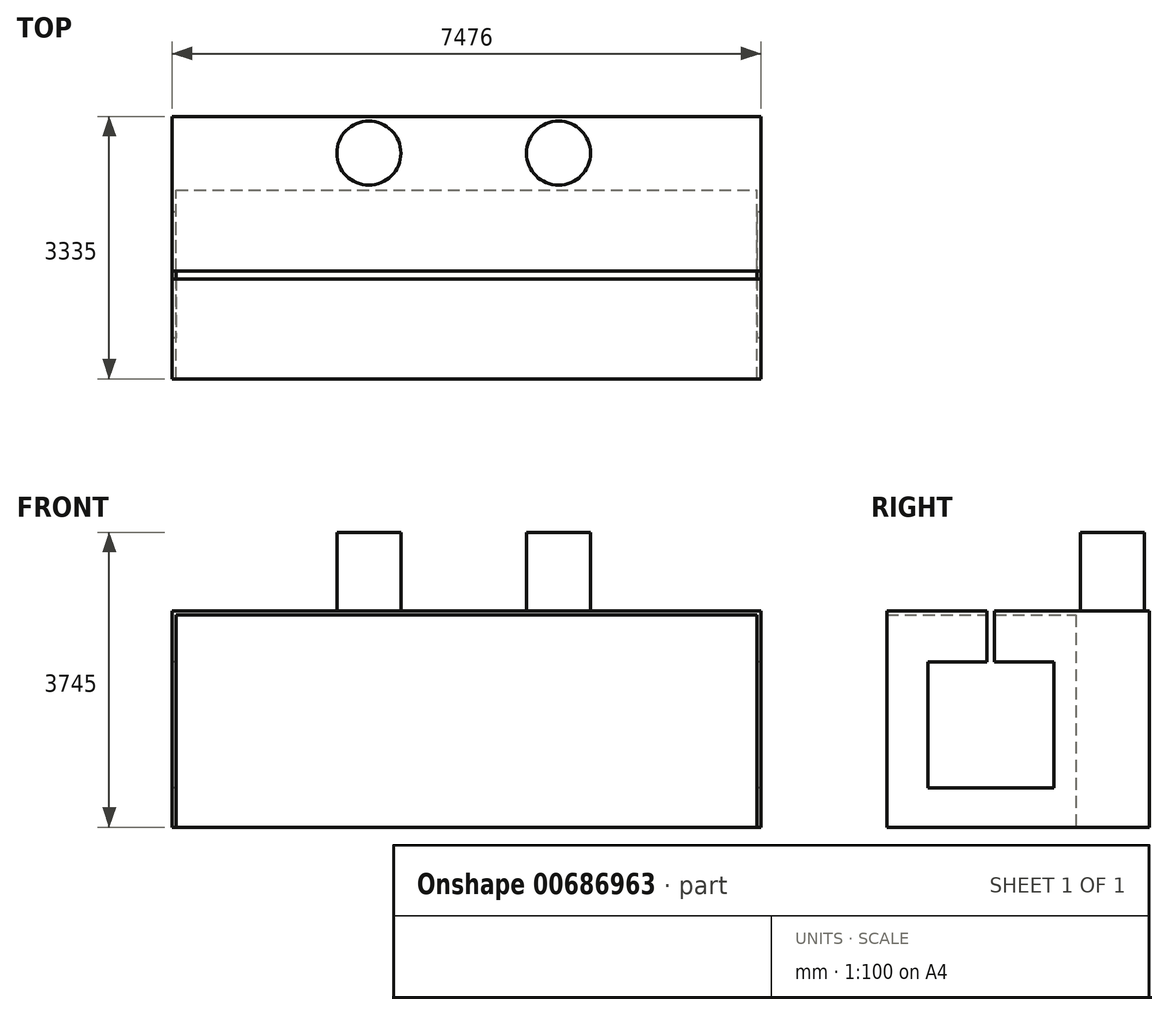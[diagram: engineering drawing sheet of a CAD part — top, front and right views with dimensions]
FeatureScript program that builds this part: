
annotation { "Feature Type Name" : "Feature", "Feature Type Description" : "" }
export const myFeature = defineFeature(function(context is Context, id is Id, definition is map)
    precondition{}
    {
        {
            var Q0;
            Q0=qCreatedBy(makeId("Front.planeOp"),FACE);
            var sketch = newSketch(context, id + "F0", { "sketchPlane" : qUnion([Q0])});
            skLineSegment(sketch, "E0.bottom", {"start": v(0, 0) * mm, "end": v(7476, 0) * mm});
            skLineSegment(sketch, "E0.top", {"start": v(0, 2745) * mm, "end": v(7476, 2745) * mm});
            skLineSegment(sketch, "E0.left", {"start": v(0, 0) * mm, "end": v(0, 2745) * mm});
            skLineSegment(sketch, "E0.right", {"start": v(7476, 0) * mm, "end": v(7476, 2745) * mm});
            skSolve(sketch);
        }
        {
            var Q0;
            Q0=makeQuery(id+"F0.imprint","IMPRINT",FACE,{"disambiguationData":[TD([[makeQuery(id+"F0.imprint","IMPRINT",EDGE,{"derivedFrom":sQuery(id+"F0.wireOp",EDGE,"E0.bottom")}),1.0]])]});
            extrude(context, id + "F1", {"entities" : qUnion([Q0]), "depth" : 935 * mm, "offsetDistance" : 25 * mm});
        }
        {
            var Q0;
            Q0=makeQuery(id+"F1.opExtrude","CAP_FACE",FACE,{"disambiguationData":[OSD([sQuery(id+"F0.wireOp",EDGE,"E0.bottom"),sQuery(id+"F0.wireOp",EDGE,"E0.top"),sQuery(id+"F0.wireOp",EDGE,"E0.left"),sQuery(id+"F0.wireOp",EDGE,"E0.right")])],"isStart":false});
            var sketch = newSketch(context, id + "F2", { "sketchPlane" : qUnion([Q0])});
            skLineSegment(sketch, "E1.bottom", {"start": v(38, 2050) * mm, "end": v(2438, 2050) * mm});
            skLineSegment(sketch, "E1.top", {"start": v(38, 250) * mm, "end": v(2438, 250) * mm});
            skLineSegment(sketch, "E1.left", {"start": v(38, 2050) * mm, "end": v(38, 250) * mm});
            skLineSegment(sketch, "E1.right", {"start": v(2438, 2050) * mm, "end": v(2438, 250) * mm});
            skLineSegment(sketch, "E2.1.0.0", {"start": v(2538, 250) * mm, "end": v(4938, 250) * mm});
            skLineSegment(sketch, "E2.1.0.1", {"start": v(2538, 2050) * mm, "end": v(4938, 2050) * mm});
            skLineSegment(sketch, "E2.1.0.2", {"start": v(4938, 2050) * mm, "end": v(4938, 250) * mm});
            skLineSegment(sketch, "E2.1.0.3", {"start": v(2538, 2050) * mm, "end": v(2538, 250) * mm});
            skLineSegment(sketch, "E2.2.0.0", {"start": v(5038, 250) * mm, "end": v(7438, 250) * mm});
            skLineSegment(sketch, "E2.2.0.1", {"start": v(5038, 2050) * mm, "end": v(7438, 2050) * mm});
            skLineSegment(sketch, "E2.2.0.2", {"start": v(7438, 2050) * mm, "end": v(7438, 250) * mm});
            skLineSegment(sketch, "E2.2.0.3", {"start": v(5038, 2050) * mm, "end": v(5038, 250) * mm});
            skLineSegment(sketch, "E2.direction1", {"start": v(38, 2050) * mm, "end": v(2538, 2050) * mm, "construction": true});
            skLineSegment(sketch, "E3.1.0.0", {"start": v(63, 2050) * mm, "end": v(63, 250) * mm});
            skLineSegment(sketch, "E3.2.0.0", {"start": v(88, 2050) * mm, "end": v(88, 250) * mm});
            skLineSegment(sketch, "E3.3.0.0", {"start": v(113, 2050) * mm, "end": v(113, 250) * mm});
            skLineSegment(sketch, "E3.4.0.0", {"start": v(138, 2050) * mm, "end": v(138, 250) * mm});
            skLineSegment(sketch, "E3.5.0.0", {"start": v(163, 2050) * mm, "end": v(163, 250) * mm});
            skLineSegment(sketch, "E3.6.0.0", {"start": v(188, 2050) * mm, "end": v(188, 250) * mm});
            skLineSegment(sketch, "E3.7.0.0", {"start": v(213, 2050) * mm, "end": v(213, 250) * mm});
            skLineSegment(sketch, "E3.8.0.0", {"start": v(238, 2050) * mm, "end": v(238, 250) * mm});
            skLineSegment(sketch, "E3.9.0.0", {"start": v(263, 2050) * mm, "end": v(263, 250) * mm});
            skLineSegment(sketch, "E3.10.0.0", {"start": v(288, 2050) * mm, "end": v(288, 250) * mm});
            skLineSegment(sketch, "E3.11.0.0", {"start": v(313, 2050) * mm, "end": v(313, 250) * mm});
            skLineSegment(sketch, "E3.12.0.0", {"start": v(338, 2050) * mm, "end": v(338, 250) * mm});
            skLineSegment(sketch, "E3.13.0.0", {"start": v(363, 2050) * mm, "end": v(363, 250) * mm});
            skLineSegment(sketch, "E3.14.0.0", {"start": v(388, 2050) * mm, "end": v(388, 250) * mm});
            skLineSegment(sketch, "E3.15.0.0", {"start": v(413, 2050) * mm, "end": v(413, 250) * mm});
            skLineSegment(sketch, "E3.16.0.0", {"start": v(438, 2050) * mm, "end": v(438, 250) * mm});
            skLineSegment(sketch, "E3.17.0.0", {"start": v(463, 2050) * mm, "end": v(463, 250) * mm});
            skLineSegment(sketch, "E3.18.0.0", {"start": v(488, 2050) * mm, "end": v(488, 250) * mm});
            skLineSegment(sketch, "E3.19.0.0", {"start": v(513, 2050) * mm, "end": v(513, 250) * mm});
            skLineSegment(sketch, "E3.20.0.0", {"start": v(538, 2050) * mm, "end": v(538, 250) * mm});
            skLineSegment(sketch, "E3.21.0.0", {"start": v(563, 2050) * mm, "end": v(563, 250) * mm});
            skLineSegment(sketch, "E3.22.0.0", {"start": v(588, 2050) * mm, "end": v(588, 250) * mm});
            skLineSegment(sketch, "E3.23.0.0", {"start": v(613, 2050) * mm, "end": v(613, 250) * mm});
            skLineSegment(sketch, "E3.24.0.0", {"start": v(638, 2050) * mm, "end": v(638, 250) * mm});
            skLineSegment(sketch, "E3.25.0.0", {"start": v(663, 2050) * mm, "end": v(663, 250) * mm});
            skLineSegment(sketch, "E3.26.0.0", {"start": v(688, 2050) * mm, "end": v(688, 250) * mm});
            skLineSegment(sketch, "E3.27.0.0", {"start": v(713, 2050) * mm, "end": v(713, 250) * mm});
            skLineSegment(sketch, "E3.28.0.0", {"start": v(738, 2050) * mm, "end": v(738, 250) * mm});
            skLineSegment(sketch, "E3.29.0.0", {"start": v(763, 2050) * mm, "end": v(763, 250) * mm});
            skLineSegment(sketch, "E3.30.0.0", {"start": v(788, 2050) * mm, "end": v(788, 250) * mm});
            skLineSegment(sketch, "E3.31.0.0", {"start": v(813, 2050) * mm, "end": v(813, 250) * mm});
            skLineSegment(sketch, "E3.32.0.0", {"start": v(838, 2050) * mm, "end": v(838, 250) * mm});
            skLineSegment(sketch, "E3.33.0.0", {"start": v(863, 2050) * mm, "end": v(863, 250) * mm});
            skLineSegment(sketch, "E3.34.0.0", {"start": v(888, 2050) * mm, "end": v(888, 250) * mm});
            skLineSegment(sketch, "E3.35.0.0", {"start": v(913, 2050) * mm, "end": v(913, 250) * mm});
            skLineSegment(sketch, "E3.36.0.0", {"start": v(938, 2050) * mm, "end": v(938, 250) * mm});
            skLineSegment(sketch, "E3.37.0.0", {"start": v(963, 2050) * mm, "end": v(963, 250) * mm});
            skLineSegment(sketch, "E3.38.0.0", {"start": v(988, 2050) * mm, "end": v(988, 250) * mm});
            skLineSegment(sketch, "E3.39.0.0", {"start": v(1013, 2050) * mm, "end": v(1013, 250) * mm});
            skLineSegment(sketch, "E3.40.0.0", {"start": v(1038, 2050) * mm, "end": v(1038, 250) * mm});
            skLineSegment(sketch, "E3.41.0.0", {"start": v(1063, 2050) * mm, "end": v(1063, 250) * mm});
            skLineSegment(sketch, "E3.42.0.0", {"start": v(1088, 2050) * mm, "end": v(1088, 250) * mm});
            skLineSegment(sketch, "E3.43.0.0", {"start": v(1113, 2050) * mm, "end": v(1113, 250) * mm});
            skLineSegment(sketch, "E3.44.0.0", {"start": v(1138, 2050) * mm, "end": v(1138, 250) * mm});
            skLineSegment(sketch, "E3.45.0.0", {"start": v(1163, 2050) * mm, "end": v(1163, 250) * mm});
            skLineSegment(sketch, "E3.46.0.0", {"start": v(1188, 2050) * mm, "end": v(1188, 250) * mm});
            skLineSegment(sketch, "E3.47.0.0", {"start": v(1213, 2050) * mm, "end": v(1213, 250) * mm});
            skLineSegment(sketch, "E3.48.0.0", {"start": v(1238, 2050) * mm, "end": v(1238, 250) * mm});
            skLineSegment(sketch, "E3.49.0.0", {"start": v(1263, 2050) * mm, "end": v(1263, 250) * mm});
            skLineSegment(sketch, "E3.50.0.0", {"start": v(1288, 2050) * mm, "end": v(1288, 250) * mm});
            skLineSegment(sketch, "E3.51.0.0", {"start": v(1313, 2050) * mm, "end": v(1313, 250) * mm});
            skLineSegment(sketch, "E3.52.0.0", {"start": v(1338, 2050) * mm, "end": v(1338, 250) * mm});
            skLineSegment(sketch, "E3.53.0.0", {"start": v(1363, 2050) * mm, "end": v(1363, 250) * mm});
            skLineSegment(sketch, "E3.54.0.0", {"start": v(1388, 2050) * mm, "end": v(1388, 250) * mm});
            skLineSegment(sketch, "E3.55.0.0", {"start": v(1413, 2050) * mm, "end": v(1413, 250) * mm});
            skLineSegment(sketch, "E3.56.0.0", {"start": v(1438, 2050) * mm, "end": v(1438, 250) * mm});
            skLineSegment(sketch, "E3.57.0.0", {"start": v(1463, 2050) * mm, "end": v(1463, 250) * mm});
            skLineSegment(sketch, "E3.58.0.0", {"start": v(1488, 2050) * mm, "end": v(1488, 250) * mm});
            skLineSegment(sketch, "E3.59.0.0", {"start": v(1513, 2050) * mm, "end": v(1513, 250) * mm});
            skLineSegment(sketch, "E3.60.0.0", {"start": v(1538, 2050) * mm, "end": v(1538, 250) * mm});
            skLineSegment(sketch, "E3.61.0.0", {"start": v(1563, 2050) * mm, "end": v(1563, 250) * mm});
            skLineSegment(sketch, "E3.62.0.0", {"start": v(1588, 2050) * mm, "end": v(1588, 250) * mm});
            skLineSegment(sketch, "E3.63.0.0", {"start": v(1613, 2050) * mm, "end": v(1613, 250) * mm});
            skLineSegment(sketch, "E3.64.0.0", {"start": v(1638, 2050) * mm, "end": v(1638, 250) * mm});
            skLineSegment(sketch, "E3.65.0.0", {"start": v(1663, 2050) * mm, "end": v(1663, 250) * mm});
            skLineSegment(sketch, "E3.66.0.0", {"start": v(1688, 2050) * mm, "end": v(1688, 250) * mm});
            skLineSegment(sketch, "E3.67.0.0", {"start": v(1713, 2050) * mm, "end": v(1713, 250) * mm});
            skLineSegment(sketch, "E3.68.0.0", {"start": v(1738, 2050) * mm, "end": v(1738, 250) * mm});
            skLineSegment(sketch, "E3.69.0.0", {"start": v(1763, 2050) * mm, "end": v(1763, 250) * mm});
            skLineSegment(sketch, "E3.70.0.0", {"start": v(1788, 2050) * mm, "end": v(1788, 250) * mm});
            skLineSegment(sketch, "E3.71.0.0", {"start": v(1813, 2050) * mm, "end": v(1813, 250) * mm});
            skLineSegment(sketch, "E3.72.0.0", {"start": v(1838, 2050) * mm, "end": v(1838, 250) * mm});
            skLineSegment(sketch, "E3.73.0.0", {"start": v(1863, 2050) * mm, "end": v(1863, 250) * mm});
            skLineSegment(sketch, "E3.74.0.0", {"start": v(1888, 2050) * mm, "end": v(1888, 250) * mm});
            skLineSegment(sketch, "E3.75.0.0", {"start": v(1913, 2050) * mm, "end": v(1913, 250) * mm});
            skLineSegment(sketch, "E3.76.0.0", {"start": v(1938, 2050) * mm, "end": v(1938, 250) * mm});
            skLineSegment(sketch, "E3.77.0.0", {"start": v(1963, 2050) * mm, "end": v(1963, 250) * mm});
            skLineSegment(sketch, "E3.78.0.0", {"start": v(1988, 2050) * mm, "end": v(1988, 250) * mm});
            skLineSegment(sketch, "E3.79.0.0", {"start": v(2013, 2050) * mm, "end": v(2013, 250) * mm});
            skLineSegment(sketch, "E3.80.0.0", {"start": v(2038, 2050) * mm, "end": v(2038, 250) * mm});
            skLineSegment(sketch, "E3.81.0.0", {"start": v(2063, 2050) * mm, "end": v(2063, 250) * mm});
            skLineSegment(sketch, "E3.82.0.0", {"start": v(2088, 2050) * mm, "end": v(2088, 250) * mm});
            skLineSegment(sketch, "E3.83.0.0", {"start": v(2113, 2050) * mm, "end": v(2113, 250) * mm});
            skLineSegment(sketch, "E3.84.0.0", {"start": v(2138, 2050) * mm, "end": v(2138, 250) * mm});
            skLineSegment(sketch, "E3.85.0.0", {"start": v(2163, 2050) * mm, "end": v(2163, 250) * mm});
            skLineSegment(sketch, "E3.86.0.0", {"start": v(2188, 2050) * mm, "end": v(2188, 250) * mm});
            skLineSegment(sketch, "E3.87.0.0", {"start": v(2213, 2050) * mm, "end": v(2213, 250) * mm});
            skLineSegment(sketch, "E3.88.0.0", {"start": v(2238, 2050) * mm, "end": v(2238, 250) * mm});
            skLineSegment(sketch, "E3.89.0.0", {"start": v(2263, 2050) * mm, "end": v(2263, 250) * mm});
            skLineSegment(sketch, "E3.90.0.0", {"start": v(2288, 2050) * mm, "end": v(2288, 250) * mm});
            skLineSegment(sketch, "E3.91.0.0", {"start": v(2313, 2050) * mm, "end": v(2313, 250) * mm});
            skLineSegment(sketch, "E3.92.0.0", {"start": v(2338, 2050) * mm, "end": v(2338, 250) * mm});
            skLineSegment(sketch, "E3.93.0.0", {"start": v(2363, 2050) * mm, "end": v(2363, 250) * mm});
            skLineSegment(sketch, "E3.94.0.0", {"start": v(2388, 2050) * mm, "end": v(2388, 250) * mm});
            skLineSegment(sketch, "E3.direction1", {"start": v(38, 250) * mm, "end": v(63, 250) * mm, "construction": true});
            skLineSegment(sketch, "E4.0.95.0", {"start": v(2413, 2050) * mm, "end": v(2413, 250) * mm});
            skLineSegment(sketch, "E5.1.0.0", {"start": v(5063, 2050) * mm, "end": v(5063, 250) * mm});
            skLineSegment(sketch, "E5.2.0.0", {"start": v(5088, 2050) * mm, "end": v(5088, 250) * mm});
            skLineSegment(sketch, "E5.3.0.0", {"start": v(5113, 2050) * mm, "end": v(5113, 250) * mm});
            skLineSegment(sketch, "E5.4.0.0", {"start": v(5138, 2050) * mm, "end": v(5138, 250) * mm});
            skLineSegment(sketch, "E5.5.0.0", {"start": v(5163, 2050) * mm, "end": v(5163, 250) * mm});
            skLineSegment(sketch, "E5.6.0.0", {"start": v(5188, 2050) * mm, "end": v(5188, 250) * mm});
            skLineSegment(sketch, "E5.7.0.0", {"start": v(5213, 2050) * mm, "end": v(5213, 250) * mm});
            skLineSegment(sketch, "E5.8.0.0", {"start": v(5238, 2050) * mm, "end": v(5238, 250) * mm});
            skLineSegment(sketch, "E5.9.0.0", {"start": v(5263, 2050) * mm, "end": v(5263, 250) * mm});
            skLineSegment(sketch, "E5.10.0.0", {"start": v(5288, 2050) * mm, "end": v(5288, 250) * mm});
            skLineSegment(sketch, "E5.11.0.0", {"start": v(5313, 2050) * mm, "end": v(5313, 250) * mm});
            skLineSegment(sketch, "E5.12.0.0", {"start": v(5338, 2050) * mm, "end": v(5338, 250) * mm});
            skLineSegment(sketch, "E5.13.0.0", {"start": v(5363, 2050) * mm, "end": v(5363, 250) * mm});
            skLineSegment(sketch, "E5.14.0.0", {"start": v(5388, 2050) * mm, "end": v(5388, 250) * mm});
            skLineSegment(sketch, "E5.15.0.0", {"start": v(5413, 2050) * mm, "end": v(5413, 250) * mm});
            skLineSegment(sketch, "E5.16.0.0", {"start": v(5438, 2050) * mm, "end": v(5438, 250) * mm});
            skLineSegment(sketch, "E5.17.0.0", {"start": v(5463, 2050) * mm, "end": v(5463, 250) * mm});
            skLineSegment(sketch, "E5.18.0.0", {"start": v(5488, 2050) * mm, "end": v(5488, 250) * mm});
            skLineSegment(sketch, "E5.19.0.0", {"start": v(5513, 2050) * mm, "end": v(5513, 250) * mm});
            skLineSegment(sketch, "E5.20.0.0", {"start": v(5538, 2050) * mm, "end": v(5538, 250) * mm});
            skLineSegment(sketch, "E5.21.0.0", {"start": v(5563, 2050) * mm, "end": v(5563, 250) * mm});
            skLineSegment(sketch, "E5.22.0.0", {"start": v(5588, 2050) * mm, "end": v(5588, 250) * mm});
            skLineSegment(sketch, "E5.23.0.0", {"start": v(5613, 2050) * mm, "end": v(5613, 250) * mm});
            skLineSegment(sketch, "E5.24.0.0", {"start": v(5638, 2050) * mm, "end": v(5638, 250) * mm});
            skLineSegment(sketch, "E5.25.0.0", {"start": v(5663, 2050) * mm, "end": v(5663, 250) * mm});
            skLineSegment(sketch, "E5.26.0.0", {"start": v(5688, 2050) * mm, "end": v(5688, 250) * mm});
            skLineSegment(sketch, "E5.27.0.0", {"start": v(5713, 2050) * mm, "end": v(5713, 250) * mm});
            skLineSegment(sketch, "E5.28.0.0", {"start": v(5738, 2050) * mm, "end": v(5738, 250) * mm});
            skLineSegment(sketch, "E5.29.0.0", {"start": v(5763, 2050) * mm, "end": v(5763, 250) * mm});
            skLineSegment(sketch, "E5.30.0.0", {"start": v(5788, 2050) * mm, "end": v(5788, 250) * mm});
            skLineSegment(sketch, "E5.31.0.0", {"start": v(5813, 2050) * mm, "end": v(5813, 250) * mm});
            skLineSegment(sketch, "E5.32.0.0", {"start": v(5838, 2050) * mm, "end": v(5838, 250) * mm});
            skLineSegment(sketch, "E5.33.0.0", {"start": v(5863, 2050) * mm, "end": v(5863, 250) * mm});
            skLineSegment(sketch, "E5.34.0.0", {"start": v(5888, 2050) * mm, "end": v(5888, 250) * mm});
            skLineSegment(sketch, "E5.35.0.0", {"start": v(5913, 2050) * mm, "end": v(5913, 250) * mm});
            skLineSegment(sketch, "E5.36.0.0", {"start": v(5938, 2050) * mm, "end": v(5938, 250) * mm});
            skLineSegment(sketch, "E5.37.0.0", {"start": v(5963, 2050) * mm, "end": v(5963, 250) * mm});
            skLineSegment(sketch, "E5.38.0.0", {"start": v(5988, 2050) * mm, "end": v(5988, 250) * mm});
            skLineSegment(sketch, "E5.39.0.0", {"start": v(6013, 2050) * mm, "end": v(6013, 250) * mm});
            skLineSegment(sketch, "E5.40.0.0", {"start": v(6038, 2050) * mm, "end": v(6038, 250) * mm});
            skLineSegment(sketch, "E5.41.0.0", {"start": v(6063, 2050) * mm, "end": v(6063, 250) * mm});
            skLineSegment(sketch, "E5.42.0.0", {"start": v(6088, 2050) * mm, "end": v(6088, 250) * mm});
            skLineSegment(sketch, "E5.43.0.0", {"start": v(6113, 2050) * mm, "end": v(6113, 250) * mm});
            skLineSegment(sketch, "E5.44.0.0", {"start": v(6138, 2050) * mm, "end": v(6138, 250) * mm});
            skLineSegment(sketch, "E5.45.0.0", {"start": v(6163, 2050) * mm, "end": v(6163, 250) * mm});
            skLineSegment(sketch, "E5.46.0.0", {"start": v(6188, 2050) * mm, "end": v(6188, 250) * mm});
            skLineSegment(sketch, "E5.47.0.0", {"start": v(6213, 2050) * mm, "end": v(6213, 250) * mm});
            skLineSegment(sketch, "E5.48.0.0", {"start": v(6238, 2050) * mm, "end": v(6238, 250) * mm});
            skLineSegment(sketch, "E5.49.0.0", {"start": v(6263, 2050) * mm, "end": v(6263, 250) * mm});
            skLineSegment(sketch, "E5.50.0.0", {"start": v(6288, 2050) * mm, "end": v(6288, 250) * mm});
            skLineSegment(sketch, "E5.51.0.0", {"start": v(6313, 2050) * mm, "end": v(6313, 250) * mm});
            skLineSegment(sketch, "E5.52.0.0", {"start": v(6338, 2050) * mm, "end": v(6338, 250) * mm});
            skLineSegment(sketch, "E5.53.0.0", {"start": v(6363, 2050) * mm, "end": v(6363, 250) * mm});
            skLineSegment(sketch, "E5.54.0.0", {"start": v(6388, 2050) * mm, "end": v(6388, 250) * mm});
            skLineSegment(sketch, "E5.55.0.0", {"start": v(6413, 2050) * mm, "end": v(6413, 250) * mm});
            skLineSegment(sketch, "E5.56.0.0", {"start": v(6438, 2050) * mm, "end": v(6438, 250) * mm});
            skLineSegment(sketch, "E5.57.0.0", {"start": v(6463, 2050) * mm, "end": v(6463, 250) * mm});
            skLineSegment(sketch, "E5.58.0.0", {"start": v(6488, 2050) * mm, "end": v(6488, 250) * mm});
            skLineSegment(sketch, "E5.59.0.0", {"start": v(6513, 2050) * mm, "end": v(6513, 250) * mm});
            skLineSegment(sketch, "E5.60.0.0", {"start": v(6538, 2050) * mm, "end": v(6538, 250) * mm});
            skLineSegment(sketch, "E5.61.0.0", {"start": v(6563, 2050) * mm, "end": v(6563, 250) * mm});
            skLineSegment(sketch, "E5.62.0.0", {"start": v(6588, 2050) * mm, "end": v(6588, 250) * mm});
            skLineSegment(sketch, "E5.63.0.0", {"start": v(6613, 2050) * mm, "end": v(6613, 250) * mm});
            skLineSegment(sketch, "E5.64.0.0", {"start": v(6638, 2050) * mm, "end": v(6638, 250) * mm});
            skLineSegment(sketch, "E5.65.0.0", {"start": v(6663, 2050) * mm, "end": v(6663, 250) * mm});
            skLineSegment(sketch, "E5.66.0.0", {"start": v(6688, 2050) * mm, "end": v(6688, 250) * mm});
            skLineSegment(sketch, "E5.67.0.0", {"start": v(6713, 2050) * mm, "end": v(6713, 250) * mm});
            skLineSegment(sketch, "E5.68.0.0", {"start": v(6738, 2050) * mm, "end": v(6738, 250) * mm});
            skLineSegment(sketch, "E5.69.0.0", {"start": v(6763, 2050) * mm, "end": v(6763, 250) * mm});
            skLineSegment(sketch, "E5.70.0.0", {"start": v(6788, 2050) * mm, "end": v(6788, 250) * mm});
            skLineSegment(sketch, "E5.71.0.0", {"start": v(6813, 2050) * mm, "end": v(6813, 250) * mm});
            skLineSegment(sketch, "E5.72.0.0", {"start": v(6838, 2050) * mm, "end": v(6838, 250) * mm});
            skLineSegment(sketch, "E5.73.0.0", {"start": v(6863, 2050) * mm, "end": v(6863, 250) * mm});
            skLineSegment(sketch, "E5.74.0.0", {"start": v(6888, 2050) * mm, "end": v(6888, 250) * mm});
            skLineSegment(sketch, "E5.75.0.0", {"start": v(6913, 2050) * mm, "end": v(6913, 250) * mm});
            skLineSegment(sketch, "E5.76.0.0", {"start": v(6938, 2050) * mm, "end": v(6938, 250) * mm});
            skLineSegment(sketch, "E5.77.0.0", {"start": v(6963, 2050) * mm, "end": v(6963, 250) * mm});
            skLineSegment(sketch, "E5.78.0.0", {"start": v(6988, 2050) * mm, "end": v(6988, 250) * mm});
            skLineSegment(sketch, "E5.79.0.0", {"start": v(7013, 2050) * mm, "end": v(7013, 250) * mm});
            skLineSegment(sketch, "E5.80.0.0", {"start": v(7038, 2050) * mm, "end": v(7038, 250) * mm});
            skLineSegment(sketch, "E5.81.0.0", {"start": v(7063, 2050) * mm, "end": v(7063, 250) * mm});
            skLineSegment(sketch, "E5.82.0.0", {"start": v(7088, 2050) * mm, "end": v(7088, 250) * mm});
            skLineSegment(sketch, "E5.83.0.0", {"start": v(7113, 2050) * mm, "end": v(7113, 250) * mm});
            skLineSegment(sketch, "E5.84.0.0", {"start": v(7138, 2050) * mm, "end": v(7138, 250) * mm});
            skLineSegment(sketch, "E5.85.0.0", {"start": v(7163, 2050) * mm, "end": v(7163, 250) * mm});
            skLineSegment(sketch, "E5.86.0.0", {"start": v(7188, 2050) * mm, "end": v(7188, 250) * mm});
            skLineSegment(sketch, "E5.87.0.0", {"start": v(7213, 2050) * mm, "end": v(7213, 250) * mm});
            skLineSegment(sketch, "E5.88.0.0", {"start": v(7238, 2050) * mm, "end": v(7238, 250) * mm});
            skLineSegment(sketch, "E5.89.0.0", {"start": v(7263, 2050) * mm, "end": v(7263, 250) * mm});
            skLineSegment(sketch, "E5.90.0.0", {"start": v(7288, 2050) * mm, "end": v(7288, 250) * mm});
            skLineSegment(sketch, "E5.91.0.0", {"start": v(7313, 2050) * mm, "end": v(7313, 250) * mm});
            skLineSegment(sketch, "E5.92.0.0", {"start": v(7338, 2050) * mm, "end": v(7338, 250) * mm});
            skLineSegment(sketch, "E5.93.0.0", {"start": v(7363, 2050) * mm, "end": v(7363, 250) * mm});
            skLineSegment(sketch, "E5.94.0.0", {"start": v(7388, 2050) * mm, "end": v(7388, 250) * mm});
            skLineSegment(sketch, "E5.95.0.0", {"start": v(7413, 2050) * mm, "end": v(7413, 250) * mm});
            skLineSegment(sketch, "E5.direction1", {"start": v(5038, 250) * mm, "end": v(5063, 250) * mm, "construction": true});
            skLineSegment(sketch, "E6.1.0.0", {"start": v(2563, 2050) * mm, "end": v(2563, 250) * mm});
            skLineSegment(sketch, "E6.2.0.0", {"start": v(2588, 2050) * mm, "end": v(2588, 250) * mm});
            skLineSegment(sketch, "E6.3.0.0", {"start": v(2613, 2050) * mm, "end": v(2613, 250) * mm});
            skLineSegment(sketch, "E6.4.0.0", {"start": v(2638, 2050) * mm, "end": v(2638, 250) * mm});
            skLineSegment(sketch, "E6.5.0.0", {"start": v(2663, 2050) * mm, "end": v(2663, 250) * mm});
            skLineSegment(sketch, "E6.6.0.0", {"start": v(2688, 2050) * mm, "end": v(2688, 250) * mm});
            skLineSegment(sketch, "E6.7.0.0", {"start": v(2713, 2050) * mm, "end": v(2713, 250) * mm});
            skLineSegment(sketch, "E6.8.0.0", {"start": v(2738, 2050) * mm, "end": v(2738, 250) * mm});
            skLineSegment(sketch, "E6.9.0.0", {"start": v(2763, 2050) * mm, "end": v(2763, 250) * mm});
            skLineSegment(sketch, "E6.10.0.0", {"start": v(2788, 2050) * mm, "end": v(2788, 250) * mm});
            skLineSegment(sketch, "E6.11.0.0", {"start": v(2813, 2050) * mm, "end": v(2813, 250) * mm});
            skLineSegment(sketch, "E6.12.0.0", {"start": v(2838, 2050) * mm, "end": v(2838, 250) * mm});
            skLineSegment(sketch, "E6.13.0.0", {"start": v(2863, 2050) * mm, "end": v(2863, 250) * mm});
            skLineSegment(sketch, "E6.14.0.0", {"start": v(2888, 2050) * mm, "end": v(2888, 250) * mm});
            skLineSegment(sketch, "E6.15.0.0", {"start": v(2913, 2050) * mm, "end": v(2913, 250) * mm});
            skLineSegment(sketch, "E6.16.0.0", {"start": v(2938, 2050) * mm, "end": v(2938, 250) * mm});
            skLineSegment(sketch, "E6.17.0.0", {"start": v(2963, 2050) * mm, "end": v(2963, 250) * mm});
            skLineSegment(sketch, "E6.18.0.0", {"start": v(2988, 2050) * mm, "end": v(2988, 250) * mm});
            skLineSegment(sketch, "E6.19.0.0", {"start": v(3013, 2050) * mm, "end": v(3013, 250) * mm});
            skLineSegment(sketch, "E6.20.0.0", {"start": v(3038, 2050) * mm, "end": v(3038, 250) * mm});
            skLineSegment(sketch, "E6.21.0.0", {"start": v(3063, 2050) * mm, "end": v(3063, 250) * mm});
            skLineSegment(sketch, "E6.22.0.0", {"start": v(3088, 2050) * mm, "end": v(3088, 250) * mm});
            skLineSegment(sketch, "E6.23.0.0", {"start": v(3113, 2050) * mm, "end": v(3113, 250) * mm});
            skLineSegment(sketch, "E6.24.0.0", {"start": v(3138, 2050) * mm, "end": v(3138, 250) * mm});
            skLineSegment(sketch, "E6.25.0.0", {"start": v(3163, 2050) * mm, "end": v(3163, 250) * mm});
            skLineSegment(sketch, "E6.26.0.0", {"start": v(3188, 2050) * mm, "end": v(3188, 250) * mm});
            skLineSegment(sketch, "E6.27.0.0", {"start": v(3213, 2050) * mm, "end": v(3213, 250) * mm});
            skLineSegment(sketch, "E6.28.0.0", {"start": v(3238, 2050) * mm, "end": v(3238, 250) * mm});
            skLineSegment(sketch, "E6.29.0.0", {"start": v(3263, 2050) * mm, "end": v(3263, 250) * mm});
            skLineSegment(sketch, "E6.30.0.0", {"start": v(3288, 2050) * mm, "end": v(3288, 250) * mm});
            skLineSegment(sketch, "E6.31.0.0", {"start": v(3313, 2050) * mm, "end": v(3313, 250) * mm});
            skLineSegment(sketch, "E6.32.0.0", {"start": v(3338, 2050) * mm, "end": v(3338, 250) * mm});
            skLineSegment(sketch, "E6.33.0.0", {"start": v(3363, 2050) * mm, "end": v(3363, 250) * mm});
            skLineSegment(sketch, "E6.34.0.0", {"start": v(3388, 2050) * mm, "end": v(3388, 250) * mm});
            skLineSegment(sketch, "E6.35.0.0", {"start": v(3413, 2050) * mm, "end": v(3413, 250) * mm});
            skLineSegment(sketch, "E6.36.0.0", {"start": v(3438, 2050) * mm, "end": v(3438, 250) * mm});
            skLineSegment(sketch, "E6.37.0.0", {"start": v(3463, 2050) * mm, "end": v(3463, 250) * mm});
            skLineSegment(sketch, "E6.38.0.0", {"start": v(3488, 2050) * mm, "end": v(3488, 250) * mm});
            skLineSegment(sketch, "E6.39.0.0", {"start": v(3513, 2050) * mm, "end": v(3513, 250) * mm});
            skLineSegment(sketch, "E6.40.0.0", {"start": v(3538, 2050) * mm, "end": v(3538, 250) * mm});
            skLineSegment(sketch, "E6.41.0.0", {"start": v(3563, 2050) * mm, "end": v(3563, 250) * mm});
            skLineSegment(sketch, "E6.42.0.0", {"start": v(3588, 2050) * mm, "end": v(3588, 250) * mm});
            skLineSegment(sketch, "E6.43.0.0", {"start": v(3613, 2050) * mm, "end": v(3613, 250) * mm});
            skLineSegment(sketch, "E6.44.0.0", {"start": v(3638, 2050) * mm, "end": v(3638, 250) * mm});
            skLineSegment(sketch, "E6.45.0.0", {"start": v(3663, 2050) * mm, "end": v(3663, 250) * mm});
            skLineSegment(sketch, "E6.46.0.0", {"start": v(3688, 2050) * mm, "end": v(3688, 250) * mm});
            skLineSegment(sketch, "E6.47.0.0", {"start": v(3713, 2050) * mm, "end": v(3713, 250) * mm});
            skLineSegment(sketch, "E6.48.0.0", {"start": v(3738, 2050) * mm, "end": v(3738, 250) * mm});
            skLineSegment(sketch, "E6.49.0.0", {"start": v(3763, 2050) * mm, "end": v(3763, 250) * mm});
            skLineSegment(sketch, "E6.50.0.0", {"start": v(3788, 2050) * mm, "end": v(3788, 250) * mm});
            skLineSegment(sketch, "E6.51.0.0", {"start": v(3813, 2050) * mm, "end": v(3813, 250) * mm});
            skLineSegment(sketch, "E6.52.0.0", {"start": v(3838, 2050) * mm, "end": v(3838, 250) * mm});
            skLineSegment(sketch, "E6.53.0.0", {"start": v(3863, 2050) * mm, "end": v(3863, 250) * mm});
            skLineSegment(sketch, "E6.54.0.0", {"start": v(3888, 2050) * mm, "end": v(3888, 250) * mm});
            skLineSegment(sketch, "E6.55.0.0", {"start": v(3913, 2050) * mm, "end": v(3913, 250) * mm});
            skLineSegment(sketch, "E6.56.0.0", {"start": v(3938, 2050) * mm, "end": v(3938, 250) * mm});
            skLineSegment(sketch, "E6.57.0.0", {"start": v(3963, 2050) * mm, "end": v(3963, 250) * mm});
            skLineSegment(sketch, "E6.58.0.0", {"start": v(3988, 2050) * mm, "end": v(3988, 250) * mm});
            skLineSegment(sketch, "E6.59.0.0", {"start": v(4013, 2050) * mm, "end": v(4013, 250) * mm});
            skLineSegment(sketch, "E6.60.0.0", {"start": v(4038, 2050) * mm, "end": v(4038, 250) * mm});
            skLineSegment(sketch, "E6.61.0.0", {"start": v(4063, 2050) * mm, "end": v(4063, 250) * mm});
            skLineSegment(sketch, "E6.62.0.0", {"start": v(4088, 2050) * mm, "end": v(4088, 250) * mm});
            skLineSegment(sketch, "E6.63.0.0", {"start": v(4113, 2050) * mm, "end": v(4113, 250) * mm});
            skLineSegment(sketch, "E6.64.0.0", {"start": v(4138, 2050) * mm, "end": v(4138, 250) * mm});
            skLineSegment(sketch, "E6.65.0.0", {"start": v(4163, 2050) * mm, "end": v(4163, 250) * mm});
            skLineSegment(sketch, "E6.66.0.0", {"start": v(4188, 2050) * mm, "end": v(4188, 250) * mm});
            skLineSegment(sketch, "E6.67.0.0", {"start": v(4213, 2050) * mm, "end": v(4213, 250) * mm});
            skLineSegment(sketch, "E6.68.0.0", {"start": v(4238, 2050) * mm, "end": v(4238, 250) * mm});
            skLineSegment(sketch, "E6.69.0.0", {"start": v(4263, 2050) * mm, "end": v(4263, 250) * mm});
            skLineSegment(sketch, "E6.70.0.0", {"start": v(4288, 2050) * mm, "end": v(4288, 250) * mm});
            skLineSegment(sketch, "E6.71.0.0", {"start": v(4313, 2050) * mm, "end": v(4313, 250) * mm});
            skLineSegment(sketch, "E6.72.0.0", {"start": v(4338, 2050) * mm, "end": v(4338, 250) * mm});
            skLineSegment(sketch, "E6.73.0.0", {"start": v(4363, 2050) * mm, "end": v(4363, 250) * mm});
            skLineSegment(sketch, "E6.74.0.0", {"start": v(4388, 2050) * mm, "end": v(4388, 250) * mm});
            skLineSegment(sketch, "E6.75.0.0", {"start": v(4413, 2050) * mm, "end": v(4413, 250) * mm});
            skLineSegment(sketch, "E6.76.0.0", {"start": v(4438, 2050) * mm, "end": v(4438, 250) * mm});
            skLineSegment(sketch, "E6.77.0.0", {"start": v(4463, 2050) * mm, "end": v(4463, 250) * mm});
            skLineSegment(sketch, "E6.78.0.0", {"start": v(4488, 2050) * mm, "end": v(4488, 250) * mm});
            skLineSegment(sketch, "E6.79.0.0", {"start": v(4513, 2050) * mm, "end": v(4513, 250) * mm});
            skLineSegment(sketch, "E6.80.0.0", {"start": v(4538, 2050) * mm, "end": v(4538, 250) * mm});
            skLineSegment(sketch, "E6.81.0.0", {"start": v(4563, 2050) * mm, "end": v(4563, 250) * mm});
            skLineSegment(sketch, "E6.82.0.0", {"start": v(4588, 2050) * mm, "end": v(4588, 250) * mm});
            skLineSegment(sketch, "E6.83.0.0", {"start": v(4613, 2050) * mm, "end": v(4613, 250) * mm});
            skLineSegment(sketch, "E6.84.0.0", {"start": v(4638, 2050) * mm, "end": v(4638, 250) * mm});
            skLineSegment(sketch, "E6.85.0.0", {"start": v(4663, 2050) * mm, "end": v(4663, 250) * mm});
            skLineSegment(sketch, "E6.86.0.0", {"start": v(4688, 2050) * mm, "end": v(4688, 250) * mm});
            skLineSegment(sketch, "E6.87.0.0", {"start": v(4713, 2050) * mm, "end": v(4713, 250) * mm});
            skLineSegment(sketch, "E6.88.0.0", {"start": v(4738, 2050) * mm, "end": v(4738, 250) * mm});
            skLineSegment(sketch, "E6.89.0.0", {"start": v(4763, 2050) * mm, "end": v(4763, 250) * mm});
            skLineSegment(sketch, "E6.90.0.0", {"start": v(4788, 2050) * mm, "end": v(4788, 250) * mm});
            skLineSegment(sketch, "E6.91.0.0", {"start": v(4813, 2050) * mm, "end": v(4813, 250) * mm});
            skLineSegment(sketch, "E6.92.0.0", {"start": v(4838, 2050) * mm, "end": v(4838, 250) * mm});
            skLineSegment(sketch, "E6.93.0.0", {"start": v(4863, 2050) * mm, "end": v(4863, 250) * mm});
            skLineSegment(sketch, "E6.94.0.0", {"start": v(4888, 2050) * mm, "end": v(4888, 250) * mm});
            skLineSegment(sketch, "E6.95.0.0", {"start": v(4913, 2050) * mm, "end": v(4913, 250) * mm});
            skLineSegment(sketch, "E6.direction1", {"start": v(2538, 250) * mm, "end": v(2563, 250) * mm, "construction": true});
            skSolve(sketch);
        }
        {
            var Q0;
            Q0=makeQuery(id+"F1.opExtrude","SWEPT_FACE",FACE,{"disambiguationData":[OSD([sQuery(id+"F0.wireOp",EDGE,"E0.top")])]});
            var sketch = newSketch(context, id + "F3", { "sketchPlane" : qUnion([Q0])});
            skCircle(sketch, "E7", {"center": v(2496.92, -468) * mm, "radius": 406.5 * mm});
            skCircle(sketch, "E8", {"center": v(4906.92, -468) * mm, "radius": 406.5 * mm});
            skSolve(sketch);
        }
        {
            var Q0;
            Q0 = qSketchRegion(id + "F3", true);
            extrude(context, id + "F4", {"entities" : qUnion([Q0]), "operationType" : NewBodyOperationType.ADD, "depth" : 1000 * mm, "offsetDistance" : 25 * mm});
        }
        {
            var Q0;
            {var subQ464=sQuery(id+"F2.wireOp",EDGE,"E1.left");Q0=makeQuery(id+"F2.imprint","IMPRINT",FACE,{"disambiguationData":[TD([[makeQuery(id+"F2.imprint","IMPRINT",EDGE,{"derivedFrom":subQ464}),-1.0]])]});}
            var sketch = newSketch(context, id + "F5", { "sketchPlane" : qUnion([Q0])});
            skLineSegment(sketch, "E9", {"start": v(0, 0) * mm, "end": v(0, 2745) * mm});
            skLineSegment(sketch, "E10", {"start": v(0, 2745) * mm, "end": v(7476, 2745) * mm});
            skLineSegment(sketch, "E11", {"start": v(7476, 2745) * mm, "end": v(7476, 0) * mm});
            skLineSegment(sketch, "E12", {"start": v(0, 0) * mm, "end": v(50, 0) * mm});
            skLineSegment(sketch, "E13", {"start": v(50, 0) * mm, "end": v(50, 2695) * mm});
            skLineSegment(sketch, "E14", {"start": v(50, 2695) * mm, "end": v(7426, 2695) * mm});
            skLineSegment(sketch, "E15", {"start": v(7426, 2695) * mm, "end": v(7426, 0) * mm});
            skLineSegment(sketch, "E16", {"start": v(7426, 0) * mm, "end": v(7476, 0) * mm});
            skSolve(sketch);
        }
        {
            var Q0;
            Q0 = qSketchRegion(id + "F5", true);
            extrude(context, id + "F6", {"entities" : qUnion([Q0]), "operationType" : NewBodyOperationType.ADD, "depth" : 2400 * mm, "offsetDistance" : 25 * mm});
        }
        {
            var Q0;
            Q0=makeQuery(id+"F6.boolean.opBoolean","MERGE",FACE,{"derivedFrom":[makeQuery(id+"F1.opExtrude","SWEPT_FACE",FACE,{"disambiguationData":[OSD([sQuery(id+"F0.wireOp",EDGE,"E0.left")])]}),makeQuery(id+"F6.opExtrude","SWEPT_FACE",FACE,{"disambiguationData":[OSD([sQuery(id+"F5.wireOp",EDGE,"E9")])]})]});
            var sketch = newSketch(context, id + "F7", { "sketchPlane" : qUnion([Q0])});
            skLineSegment(sketch, "E17", {"start": v(1965.12, 2745) * mm, "end": v(1965.12, 2100) * mm});
            skLineSegment(sketch, "E18", {"start": v(1965.12, 2100) * mm, "end": v(1215.12, 2100) * mm});
            skLineSegment(sketch, "E19", {"start": v(1215.12, 2100) * mm, "end": v(1215.12, 500) * mm});
            skLineSegment(sketch, "E20", {"start": v(1215.12, 500) * mm, "end": v(2815.12, 500) * mm});
            skLineSegment(sketch, "E21", {"start": v(2815.12, 500) * mm, "end": v(2815.12, 2100) * mm});
            skLineSegment(sketch, "E22", {"start": v(2815.12, 2100) * mm, "end": v(2065.12, 2100) * mm});
            skLineSegment(sketch, "E23", {"start": v(2065.12, 2100) * mm, "end": v(2065.12, 2745) * mm});
            skLineSegment(sketch, "E24", {"start": v(2065.12, 2745) * mm, "end": v(1965.12, 2745) * mm});
            skSolve(sketch);
        }
        {
            var Q0;
            Q0 = qSketchRegion(id + "F7", true);
            extrude(context, id + "F8", {"entities" : qUnion([Q0]), "operationType" : NewBodyOperationType.REMOVE, "endBound" : BoundingType.THROUGH_ALL, "oppositeDirection" : true, "depth" : 25 * mm, "offsetDistance" : 25 * mm});
        }
    });
